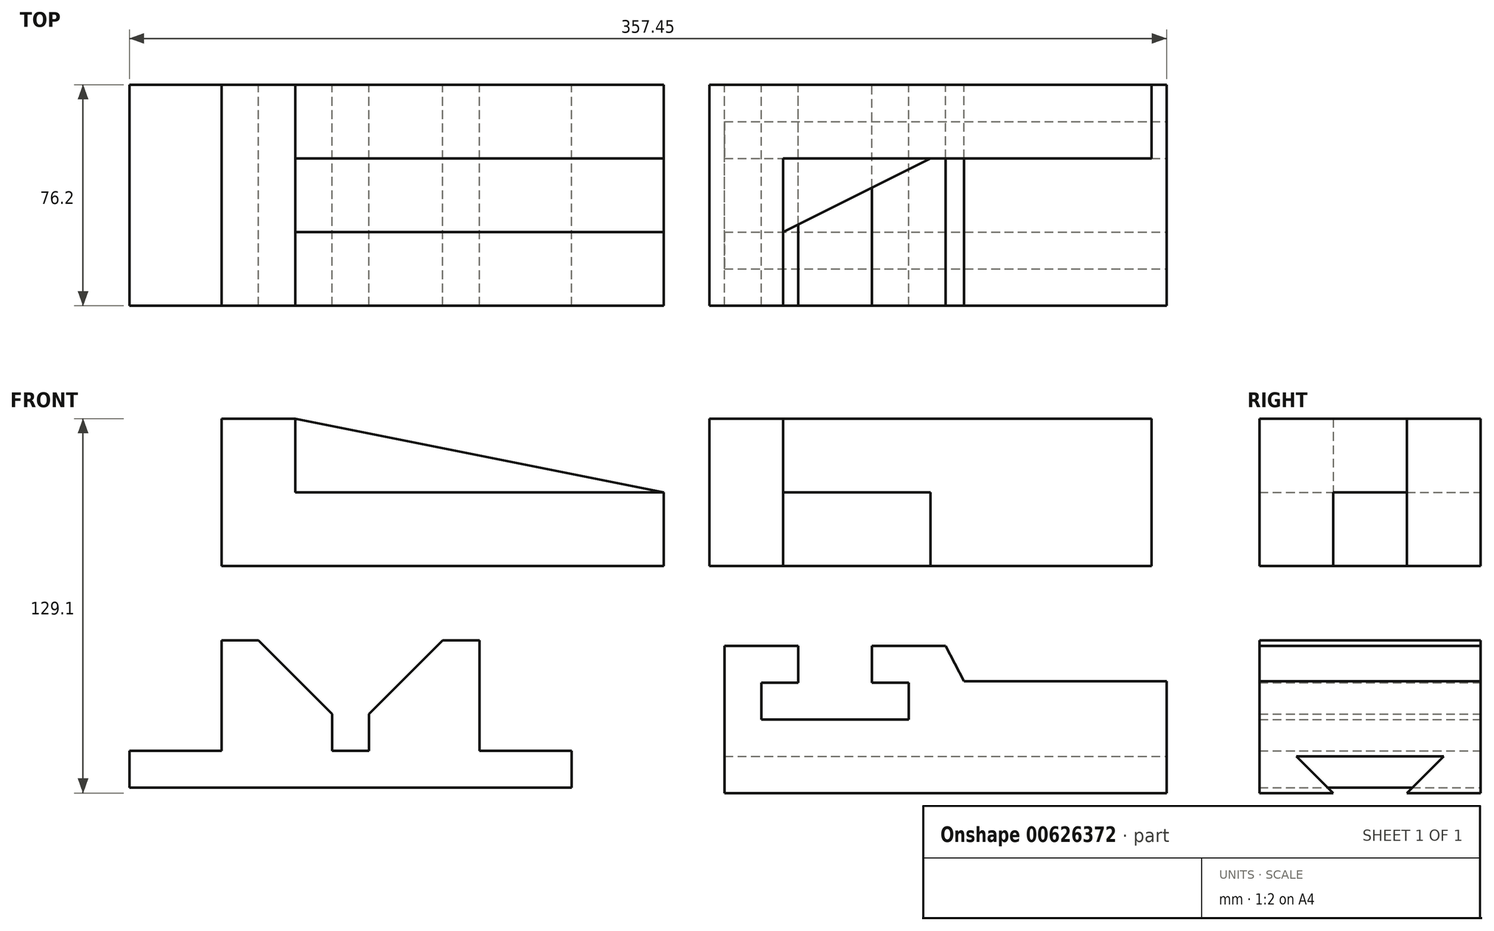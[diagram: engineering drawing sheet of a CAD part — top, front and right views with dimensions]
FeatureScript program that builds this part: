
annotation { "Feature Type Name" : "Feature", "Feature Type Description" : "" }
export const myFeature = defineFeature(function(context is Context, id is Id, definition is map)
    precondition{}
    {
        {
            var Q0;
            Q0=qCreatedBy(makeId("Front.planeOp"),FACE);
            var sketch = newSketch(context, id + "F0", { "sketchPlane" : qUnion([Q0])});
            skLineSegment(sketch, "E0", {"start": v(0, 0) * mm, "end": v(152.4, 0) * mm});
            skLineSegment(sketch, "E1", {"start": v(152.4, 0) * mm, "end": v(152.4, 25.4) * mm});
            skLineSegment(sketch, "E2", {"start": v(152.4, 25.4) * mm, "end": v(25.4, 25.4) * mm});
            skLineSegment(sketch, "E3", {"start": v(25.4, 25.4) * mm, "end": v(25.4, 50.8) * mm});
            skLineSegment(sketch, "E4", {"start": v(25.4, 50.8) * mm, "end": v(0, 50.8) * mm});
            skLineSegment(sketch, "E5", {"start": v(0, 50.8) * mm, "end": v(0, 0) * mm});
            skLineSegment(sketch, "E6", {"start": v(25.4, 50.8) * mm, "end": v(152.4, 25.4) * mm});
            skSolve(sketch);
        }
        {
            var Q0;
            Q0=makeQuery(id+"F0.imprint","IMPRINT",FACE,{"disambiguationData":[TD([[makeQuery(id+"F0.imprint","IMPRINT",EDGE,{"derivedFrom":sQuery(id+"F0.wireOp",EDGE,"E0")}),1.0]])]});
            extrude(context, id + "F1", {"entities" : qUnion([Q0]), "depth" : 76.2 * mm, "offsetDistance" : 25.4 * mm});
        }
        {
            var Q0;
            Q0=makeQuery(id+"F0.imprint","IMPRINT",FACE,{"disambiguationData":[TD([[makeQuery(id+"F0.imprint","IMPRINT",EDGE,{"derivedFrom":sQuery(id+"F0.wireOp",EDGE,"E2")}),-1.0]])]});
            extrude(context, id + "F2", {"entities" : qUnion([Q0]), "operationType" : NewBodyOperationType.ADD, "depth" : 76.2 * mm, "offsetDistance" : 25.4 * mm});
        }
        {
            var Q0;
            {var subQ0=sQuery(id+"F0.wireOp",EDGE,"E3");var subQ1=sQuery(id+"F0.wireOp",EDGE,"E2");Q0=makeQuery(id+"F2.boolean.opBoolean","MERGE",FACE,{"derivedFrom":[makeQuery(id+"F1.opExtrude","CAP_FACE",FACE,{"disambiguationData":[OSD([sQuery(id+"F0.wireOp",EDGE,"E0"),sQuery(id+"F0.wireOp",EDGE,"E1"),subQ1,subQ0,sQuery(id+"F0.wireOp",EDGE,"E4"),sQuery(id+"F0.wireOp",EDGE,"E5")])],"isStart":false}),makeQuery(id+"F2.opExtrude","CAP_FACE",FACE,{"disambiguationData":[OSD([subQ1,subQ0,sQuery(id+"F0.wireOp",EDGE,"E6")])],"isStart":false})]});}
            var sketch = newSketch(context, id + "F3", { "sketchPlane" : qUnion([Q0])});
            skLineSegment(sketch, "E7", {"start": v(25.4, 50.8) * mm, "end": v(25.4, 25.4) * mm});
            skLineSegment(sketch, "E8", {"start": v(25.4, 25.4) * mm, "end": v(152.4, 25.4) * mm});
            skSolve(sketch);
        }
        {
            var Q0;
            Q0=makeQuery(id+"F3.imprint","IMPRINT",FACE,{"disambiguationData":[TD([[makeQuery(id+"F3.imprint","IMPRINT",EDGE,{"derivedFrom":sQuery(id+"F3.wireOp",EDGE,"E7")}),1.0]])]});
            extrude(context, id + "F4", {"entities" : qUnion([Q0]), "operationType" : NewBodyOperationType.REMOVE, "oppositeDirection" : true, "depth" : 25.4 * mm, "offsetDistance" : 25.4 * mm});
        }
        {
            var Q0;
            Q0=makeQuery(id+"F0.imprint","IMPRINT",FACE,{"disambiguationData":[TD([[makeQuery(id+"F0.imprint","IMPRINT",EDGE,{"derivedFrom":sQuery(id+"F0.wireOp",EDGE,"E2")}),-1.0]])]});
            extrude(context, id + "F5", {"entities" : qUnion([Q0]), "operationType" : NewBodyOperationType.ADD, "depth" : 25.4 * mm, "offsetDistance" : 25.4 * mm});
        }
        {
            var Q0;
            Q0=makeQuery(id+"F0.imprint","IMPRINT",FACE,{"disambiguationData":[TD([[makeQuery(id+"F0.imprint","IMPRINT",EDGE,{"derivedFrom":sQuery(id+"F0.wireOp",EDGE,"E2")}),-1.0]])]});
            extrude(context, id + "F6", {"entities" : qUnion([Q0]), "operationType" : NewBodyOperationType.REMOVE, "depth" : 25.4 * mm, "offsetDistance" : 25.4 * mm});
        }
        {
            var Q0;
            Q0=qCreatedBy(makeId("Top.planeOp"),FACE);
            var sketch = newSketch(context, id + "F7", { "sketchPlane" : qUnion([Q0])});
            skLineSegment(sketch, "E9", {"start": v(168.11, 0) * mm, "end": v(168.11, -76.2) * mm});
            skLineSegment(sketch, "E10", {"start": v(168.11, -76.2) * mm, "end": v(193.51, -76.2) * mm});
            skLineSegment(sketch, "E11", {"start": v(193.51, -76.2) * mm, "end": v(193.51, -25.4) * mm});
            skLineSegment(sketch, "E12", {"start": v(193.51, -25.4) * mm, "end": v(320.51, -25.4) * mm});
            skLineSegment(sketch, "E13", {"start": v(320.51, -25.4) * mm, "end": v(320.51, 0) * mm});
            skLineSegment(sketch, "E14", {"start": v(320.51, 0) * mm, "end": v(168.11, 0) * mm});
            skSolve(sketch);
        }
        {
            var Q0;
            Q0=makeQuery(id+"F7.imprint","IMPRINT",FACE,{"disambiguationData":[TD([[makeQuery(id+"F7.imprint","IMPRINT",EDGE,{"derivedFrom":sQuery(id+"F7.wireOp",EDGE,"E9")}),1.0]])]});
            extrude(context, id + "F8", {"entities" : qUnion([Q0]), "depth" : 50.8 * mm, "offsetDistance" : 25.4 * mm});
        }
        {
            var Q0;
            Q0=makeQuery(id+"F8.opExtrude","SWEPT_FACE",FACE,{"disambiguationData":[OSD([sQuery(id+"F7.wireOp",EDGE,"E12")])]});
            var sketch = newSketch(context, id + "F9", { "sketchPlane" : qUnion([Q0])});
            skLineSegment(sketch, "E15", {"start": v(193.51, 25.4) * mm, "end": v(244.31, 25.4) * mm});
            skLineSegment(sketch, "E16", {"start": v(244.31, 25.4) * mm, "end": v(244.31, 0) * mm});
            skLineSegment(sketch, "E17", {"start": v(244.31, 0) * mm, "end": v(193.51, 0) * mm});
            skLineSegment(sketch, "E18", {"start": v(193.51, 0) * mm, "end": v(193.51, 25.4) * mm});
            skSolve(sketch);
        }
        {
            var Q0;
            Q0=makeQuery(id+"F9.imprint","IMPRINT",FACE,{"disambiguationData":[TD([[makeQuery(id+"F9.imprint","IMPRINT",EDGE,{"derivedFrom":sQuery(id+"F9.wireOp",EDGE,"E15")}),-1.0]])]});
            extrude(context, id + "F10", {"entities" : qUnion([Q0]), "operationType" : NewBodyOperationType.ADD, "depth" : 25.4 * mm, "offsetDistance" : 25.4 * mm});
        }
        {
            var Q0;
            Q0=makeQuery(id+"F10.opExtrude","SWEPT_FACE",FACE,{"disambiguationData":[OSD([sQuery(id+"F9.wireOp",EDGE,"E15")])]});
            var sketch = newSketch(context, id + "F11", { "sketchPlane" : qUnion([Q0])});
            skLineSegment(sketch, "E19", {"start": v(193.51, -50.8) * mm, "end": v(244.31, -25.4) * mm});
            skLineSegment(sketch, "E20", {"start": v(244.31, -25.4) * mm, "end": v(244.31, -50.8) * mm});
            skLineSegment(sketch, "E21", {"start": v(244.31, -50.8) * mm, "end": v(193.51, -50.8) * mm});
            skSolve(sketch);
        }
        {
            var Q0;
            Q0=makeQuery(id+"F11.imprint","IMPRINT",FACE,{"disambiguationData":[TD([[makeQuery(id+"F11.imprint","IMPRINT",EDGE,{"derivedFrom":sQuery(id+"F11.wireOp",EDGE,"E19")}),-1.0]])]});
            extrude(context, id + "F12", {"entities" : qUnion([Q0]), "operationType" : NewBodyOperationType.REMOVE, "oppositeDirection" : true, "depth" : 25.4 * mm, "offsetDistance" : 25.4 * mm});
        }
        {
            var Q0;
            Q0=qCreatedBy(makeId("Front.planeOp"),FACE);
            var sketch = newSketch(context, id + "F13", { "sketchPlane" : qUnion([Q0])});
            skLineSegment(sketch, "E22", {"start": v(120.65, -76.48) * mm, "end": v(120.65, -63.78) * mm});
            skLineSegment(sketch, "E23", {"start": v(120.65, -63.78) * mm, "end": v(88.9, -63.78) * mm});
            skLineSegment(sketch, "E24", {"start": v(88.9, -63.78) * mm, "end": v(88.9, -25.68) * mm});
            skLineSegment(sketch, "E25", {"start": v(88.9, -25.68) * mm, "end": v(76.2, -25.68) * mm});
            skLineSegment(sketch, "E26", {"start": v(76.2, -25.68) * mm, "end": v(50.8, -51.08) * mm});
            skLineSegment(sketch, "E27", {"start": v(50.8, -51.08) * mm, "end": v(50.8, -63.78) * mm});
            skLineSegment(sketch, "E28", {"start": v(50.8, -63.78) * mm, "end": v(38.1, -63.78) * mm});
            skLineSegment(sketch, "E29", {"start": v(38.1, -63.78) * mm, "end": v(38.1, -51.08) * mm});
            skLineSegment(sketch, "E30", {"start": v(38.1, -51.08) * mm, "end": v(12.7, -25.68) * mm});
            skLineSegment(sketch, "E31", {"start": v(12.7, -25.68) * mm, "end": v(0, -25.68) * mm});
            skLineSegment(sketch, "E32", {"start": v(0, -25.68) * mm, "end": v(0, -63.78) * mm});
            skLineSegment(sketch, "E33", {"start": v(0, -63.78) * mm, "end": v(-31.75, -63.78) * mm});
            skLineSegment(sketch, "E34", {"start": v(-31.75, -63.78) * mm, "end": v(-31.75, -76.48) * mm});
            skLineSegment(sketch, "E35", {"start": v(-31.75, -76.48) * mm, "end": v(120.65, -76.48) * mm});
            skSolve(sketch);
        }
        {
            var Q0;
            Q0=makeQuery(id+"F13.imprint","IMPRINT",FACE,{"disambiguationData":[TD([[makeQuery(id+"F13.imprint","IMPRINT",EDGE,{"derivedFrom":sQuery(id+"F13.wireOp",EDGE,"E22")}),1.0]])]});
            extrude(context, id + "F14", {"entities" : qUnion([Q0]), "depth" : 76.2 * mm, "offsetDistance" : 25.4 * mm});
        }
        {
            var Q0;
            Q0=qCreatedBy(makeId("Front.planeOp"),FACE);
            var sketch = newSketch(context, id + "F15", { "sketchPlane" : qUnion([Q0])});
            skLineSegment(sketch, "E36", {"start": v(173.3, -78.3) * mm, "end": v(173.3, -27.5) * mm});
            skLineSegment(sketch, "E37", {"start": v(173.3, -27.5) * mm, "end": v(198.7, -27.5) * mm});
            skLineSegment(sketch, "E38", {"start": v(198.7, -27.5) * mm, "end": v(198.7, -40.2) * mm});
            skLineSegment(sketch, "E39", {"start": v(198.7, -40.2) * mm, "end": v(186, -40.2) * mm});
            skLineSegment(sketch, "E40", {"start": v(186, -40.2) * mm, "end": v(186, -52.9) * mm});
            skLineSegment(sketch, "E41", {"start": v(186, -52.9) * mm, "end": v(236.8, -52.9) * mm});
            skLineSegment(sketch, "E42", {"start": v(236.8, -52.9) * mm, "end": v(236.8, -40.2) * mm});
            skLineSegment(sketch, "E43", {"start": v(236.8, -40.2) * mm, "end": v(224.1, -40.2) * mm});
            skLineSegment(sketch, "E44", {"start": v(224.1, -40.2) * mm, "end": v(224.1, -27.5) * mm});
            skLineSegment(sketch, "E45", {"start": v(224.1, -27.5) * mm, "end": v(249.5, -27.5) * mm});
            skLineSegment(sketch, "E46", {"start": v(249.5, -27.5) * mm, "end": v(255.85, -39.78) * mm});
            skLineSegment(sketch, "E47", {"start": v(255.85, -39.78) * mm, "end": v(325.7, -39.78) * mm});
            skLineSegment(sketch, "E48", {"start": v(325.7, -39.78) * mm, "end": v(325.7, -78.3) * mm});
            skLineSegment(sketch, "E49", {"start": v(325.7, -78.3) * mm, "end": v(173.3, -78.3) * mm});
            skSolve(sketch);
        }
        {
            var Q0;
            Q0=makeQuery(id+"F15.imprint","IMPRINT",FACE,{"disambiguationData":[TD([[makeQuery(id+"F15.imprint","IMPRINT",EDGE,{"derivedFrom":sQuery(id+"F15.wireOp",EDGE,"E36")}),-1.0]])]});
            extrude(context, id + "F16", {"entities" : qUnion([Q0]), "depth" : 76.2 * mm, "offsetDistance" : 25.4 * mm});
        }
        {
            var Q0;
            Q0=makeQuery(id+"F16.opExtrude","SWEPT_FACE",FACE,{"disambiguationData":[OSD([sQuery(id+"F15.wireOp",EDGE,"E48")])]});
            var sketch = newSketch(context, id + "F17", { "sketchPlane" : qUnion([Q0])});
            skLineSegment(sketch, "E50", {"start": v(-50.8, -78.3) * mm, "end": v(-63.5, -65.6) * mm});
            skLineSegment(sketch, "E51", {"start": v(-63.5, -65.6) * mm, "end": v(-12.7, -65.6) * mm});
            skLineSegment(sketch, "E52", {"start": v(-12.7, -65.6) * mm, "end": v(-25.4, -78.3) * mm});
            skLineSegment(sketch, "E53", {"start": v(-25.4, -78.3) * mm, "end": v(-50.8, -78.3) * mm});
            skSolve(sketch);
        }
        {
            var Q0;
            Q0=makeQuery(id+"F17.imprint","IMPRINT",FACE,{"disambiguationData":[TD([[makeQuery(id+"F17.imprint","IMPRINT",EDGE,{"derivedFrom":sQuery(id+"F17.wireOp",EDGE,"E50")}),-1.0]])]});
            extrude(context, id + "F18", {"entities" : qUnion([Q0]), "operationType" : NewBodyOperationType.REMOVE, "oppositeDirection" : true, "depth" : 152.4 * mm, "offsetDistance" : 25.4 * mm});
        }
    });
